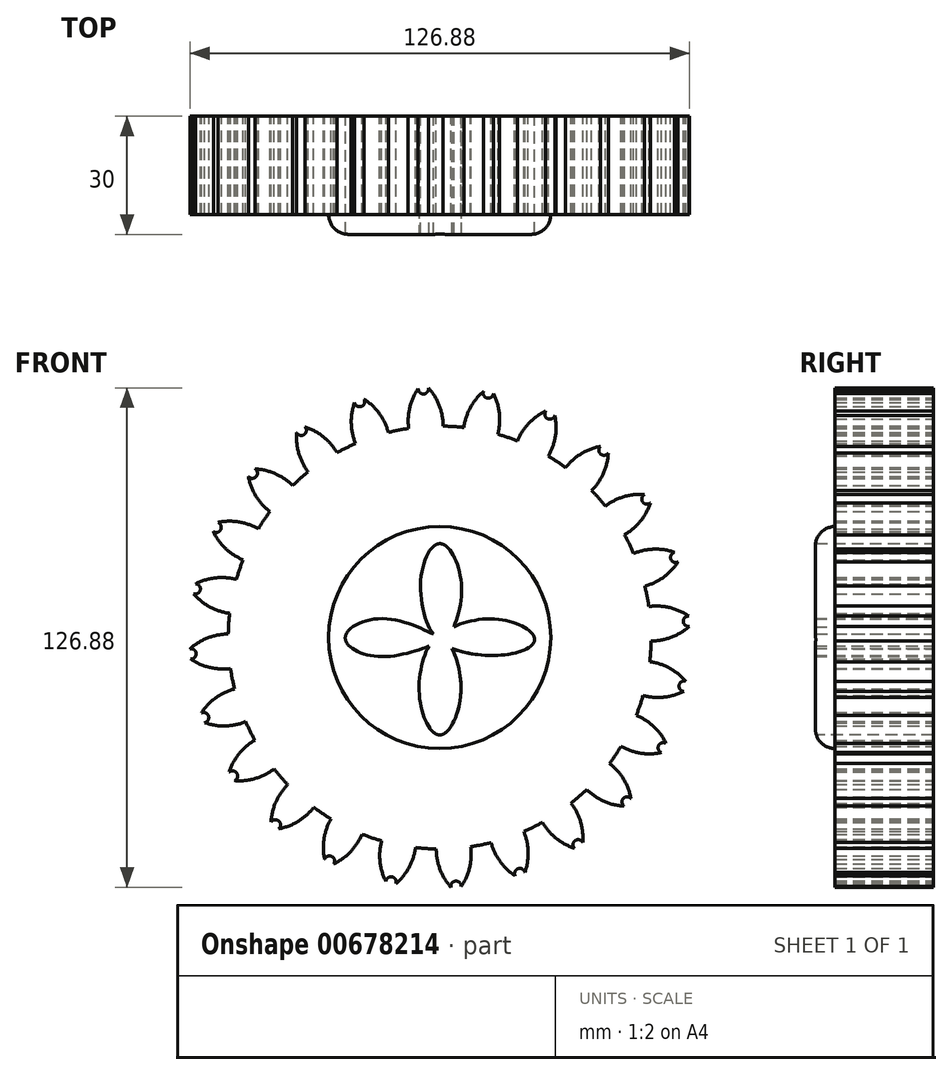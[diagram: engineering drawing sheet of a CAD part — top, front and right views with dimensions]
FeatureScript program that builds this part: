
annotation { "Feature Type Name" : "Feature", "Feature Type Description" : "" }
export const myFeature = defineFeature(function(context is Context, id is Id, definition is map)
    precondition{}
    {
        {
            var Q0;
            Q0=qCreatedBy(makeId("Front.planeOp"),FACE);
            var sketch = newSketch(context, id + "F0", { "sketchPlane" : qUnion([Q0])});
            skCircle(sketch, "E0", {"center": v(0, 0) * mm, "radius": 53.72 * mm});
            skCircle(sketch, "E1", {"center": v(0, 0) * mm, "radius": 58.67 * mm, "construction": true});
            skCircle(sketch, "E2", {"center": v(0, 0) * mm, "radius": 63.5 * mm, "construction": true});
            skLineSegment(sketch, "E3", {"start": v(0, 0) * mm, "end": v(0, 79.57) * mm, "construction": true});
            skLineSegment(sketch, "E4", {"start": v(0, 0) * mm, "end": v(-6.56, 100.09) * mm, "construction": true});
            skLineSegment(sketch, "E5", {"start": v(0, 58.67) * mm, "end": v(-52.8, 58.67) * mm, "construction": true});
            skLineSegment(sketch, "E6", {"start": v(0, 58.67) * mm, "end": v(-50.4, 40.33) * mm, "construction": true});
            skCircle(sketch, "E7", {"center": v(0, 0) * mm, "radius": 55.14 * mm, "construction": true});
            skCircle(sketch, "E8", {"center": v(0, 58.67) * mm, "radius": 14.6 * mm, "construction": true});
            skCircle(sketch, "E9", {"center": v(-13.72, 53.68) * mm, "radius": 14.6 * mm, "construction": true});
            skArc(sketch, "E10", {"start": v(0, 58.67) * mm, "mid": v(-1.2, 61.2) * mm, "end": v(-2.86, 63.44) * mm});
            skArc(sketch, "E11", {"start": v(0.88, 53.71) * mm, "mid": v(0.65, 56.23) * mm, "end": v(0, 58.67) * mm});
            skArc(sketch, "E12.MirrorCS", {"start": v(-7.66, 58.17) * mm, "mid": v(-6.8, 60.83) * mm, "end": v(-5.45, 63.27) * mm});
            skArc(sketch, "E13.MirrorCS", {"start": v(-7.88, 53.14) * mm, "mid": v(-7.99, 55.67) * mm, "end": v(-7.66, 58.17) * mm});
            skArc(sketch, "E14", {"start": v(-5.45, 63.27) * mm, "mid": v(-4.06, 61.88) * mm, "end": v(-2.86, 63.44) * mm});
            skCircle(sketch, "E15", {"center": v(0, 0) * mm, "radius": 28.21 * mm});
            skFitSpline(sketch, "E16", {"points": [v(0.41, -0.45) * mm, v(0, 0) * mm, v(-14.37, 4.8) * mm, v(-24, 0) * mm, v(-14.67, -4.85) * mm, v(0.41, -0.45) * mm]});
            skFitSpline(sketch, "E17", {"points": [v(0.41, -0.45) * mm, v(14.8, -4.52) * mm, v(24.13, -0.45) * mm, v(13.08, 4.76) * mm, v(0.41, -0.45) * mm]});
            skFitSpline(sketch, "E18", {"points": [v(0.41, -0.45) * mm, v(5.53, 12.84) * mm, v(0, 23.86) * mm, v(-4.88, 13.02) * mm, v(0.41, -0.45) * mm]});
            skFitSpline(sketch, "E19", {"points": [v(0, 0) * mm, v(5.4, -13.04) * mm, v(0, -24.75) * mm, v(-5.25, -13.1) * mm, v(0, 0) * mm]});
            skSolve(sketch);
        }
        {
            var Q0;
            {var subQ0=sQuery(id+"F0.wireOp",EDGE,"E0");var subQ1=makeQuery(id+"F0.imprint","INTERSECT",VERTEX,{"derivedFrom":[subQ0,sQuery(id+"F0.wireOp",EDGE,"E11")]});Q0=makeQuery(id+"F0.imprint","IMPRINT",FACE,{"disambiguationData":[TD([[makeQuery(id+"F0.imprint","IMPRINT",EDGE,{"disambiguationData":[TD([[subQ1,-1.0]])],"derivedFrom":subQ0}),1.0]])]});}
            var Q1;
            Q1=makeQuery(id+"F0.imprint","IMPRINT",FACE,{"disambiguationData":[TD([[makeQuery(id+"F0.imprint","IMPRINT",EDGE,{"derivedFrom":sQuery(id+"F0.wireOp",EDGE,"E10")}),1.0]])]});
            extrude(context, id + "F1", {"entities" : qUnion([Q0, Q1]), "depth" : 25 * mm, "offsetDistance" : 25 * mm});
        }
        {
            var Q0;
            Q0=makeQuery(id+"F1.opExtrude","SWEPT_BODY",BODY,{"disambiguationData":[OSD([sQuery(id+"F0.wireOp",EDGE,"E0"),sQuery(id+"F0.wireOp",EDGE,"E10"),sQuery(id+"F0.wireOp",EDGE,"E11"),sQuery(id+"F0.wireOp",EDGE,"E12.MirrorCS"),sQuery(id+"F0.wireOp",EDGE,"E13.MirrorCS"),sQuery(id+"F0.wireOp",EDGE,"E14")])]});
            var Q1;
            Q1=makeQuery(id+"F1.opExtrude","SWEPT_FACE",FACE,{"disambiguationData":[OSD([sQuery(id+"F0.wireOp",EDGE,"E0")])]});
            circularPattern(context, id + "F2", {"entities" : qUnion([Q0]), "axis" : qUnion([Q1]), "angle" : 360 * degree, "instanceCount" : 24, "equalSpace" : true});
        }
        {
            var Q0;
            Q0=makeQuery(id+"F0.imprint","IMPRINT",FACE,{"disambiguationData":[TD([[makeQuery(id+"F0.imprint","IMPRINT",EDGE,{"derivedFrom":sQuery(id+"F0.wireOp",EDGE,"E15")}),1.0]])]});
            extrude(context, id + "F3", {"entities" : qUnion([Q0]), "operationType" : NewBodyOperationType.ADD, "depth" : 30 * mm, "offsetDistance" : 25 * mm});
        }
        {
            var Q0;
            Q0=makeQuery(id+"F3.opExtrude","CAP_EDGE",EDGE,{"disambiguationData":[OSD([sQuery(id+"F0.wireOp",EDGE,"E15")])],"isStart":false});
            fillet(context, id + "F4", {"entities" : qUnion([Q0]), "radius" : 5 * mm, "tangentPropagation" : true, "allowEdgeOverflow" : false});
        }
    });
